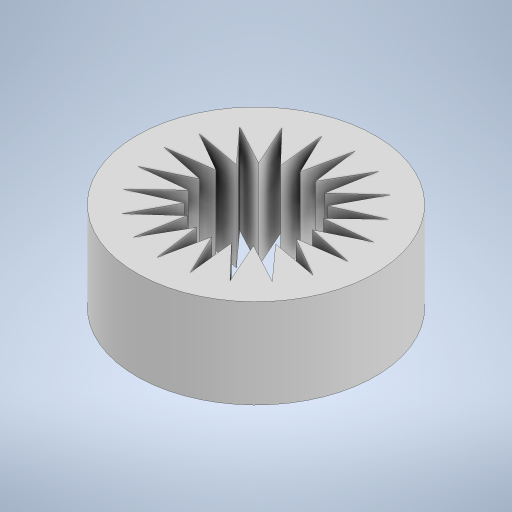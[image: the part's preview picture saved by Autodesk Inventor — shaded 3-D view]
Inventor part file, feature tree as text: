
AUTODESK INVENTOR PART (.ipt)
format: ipt  version: 2023.1 (Build 271208000, 208)  size: 274,432 bytes
history: native  units: mm
features: extrude x1, sketch x1
ambient origin geometry x8: Origin, YZ Plane, XZ Plane, XY Plane, X Axis, Y Axis, Z Axis, Center Point
bodies: Body1 (feature_tree)
feature tree (2):
  extrude  "Extrusion2"  Depth=3.0mm
  sketch  "Sketch1"  dims[d1=1.5mm d5=3.141593mm d6=0.418705mm d7=200.0mm d9=360.0deg d13=8.0mm d14=3.0mm d15=0.0mm d16=3.4mm]
